# Revit family: Plumbing-Soap-Dispensers-Sloan-Valve-ESD-700_
name_source: partatom
category: Specialty Equipment
units: mm (PartAtom-declared; Revit-internal decimal feet)

## family parameters
Cut with Voids When Loaded = No
Host = Face
Maintain Annotation Orientation = No
OmniClass Number = 23.40.20.21.34
OmniClass Title = Soap Holders, Dispensers
Part Type = Normal
Room Calculation Point = No
Round Connector Dimension = Use Diameter
Shared = No

## types (2) — shared parameters
Apparent Load = 750 VA
Assembly Code = D2010
Current = 15 A
Date Updated = 09.12.2024
Default Elevation = 0"
Depth = 5 1/4"
Edition number = 1
Height = 4 1/8"
Keynote = 15410
Manufacturer = Sloan Valve
Number of Poles = 3
Power Factor = 0.8
Product data url = https://bimobject.com
URL = www.sloanvalve.com
Version = 2
Voltage = 120 V
Width = 4 1/8"

## per-type parameters (varying)
| type | Description | Part Number | Product Material |
| ESD-700-CP | Polished Chrome Finish, Sloan® Deck-Mounted Foam Soap Dispenser. | 3346095 | Sloan Valve - Finish - Polished Chrome |
| ESD-700A-PVDBB | Brushed Brass Finish, Sloan® Deck-Mounted Foam Soap Dispenser. | 33461039 | Sloan Valve - Finish - Brushed Brass |

note: column(s) folded — value = type name in every type: Model

## geometry (parser evidence)
native form markers: Sweep x4
no freeform markers — native parametric forms only
